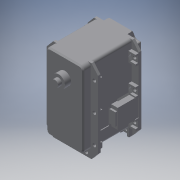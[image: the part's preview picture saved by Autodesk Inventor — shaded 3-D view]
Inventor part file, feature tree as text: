
AUTODESK INVENTOR PART (.ipt)
format: ipt  version: 2016 (Build 200138000, 138)  size: 518,144 bytes
history: native  units: in
note: dims shown in document units (in); Inventor stores cm internally (conversion verified against a paired STEP export)
features: other x3, sketch x1
ambient origin geometry x8: Origin, YZ Plane, XZ Plane, XY Plane, X Axis, Y Axis, Z Axis, Center Point
bodies: Solid1 (feature_tree)
feature tree (4):
  other  "MX-106T.ipt"
  other  "Solid1::MX-106T.ipt"
  other  "TaggingFeature1"
  sketch  "Sketch1"  dims[d0=0.3937in]
